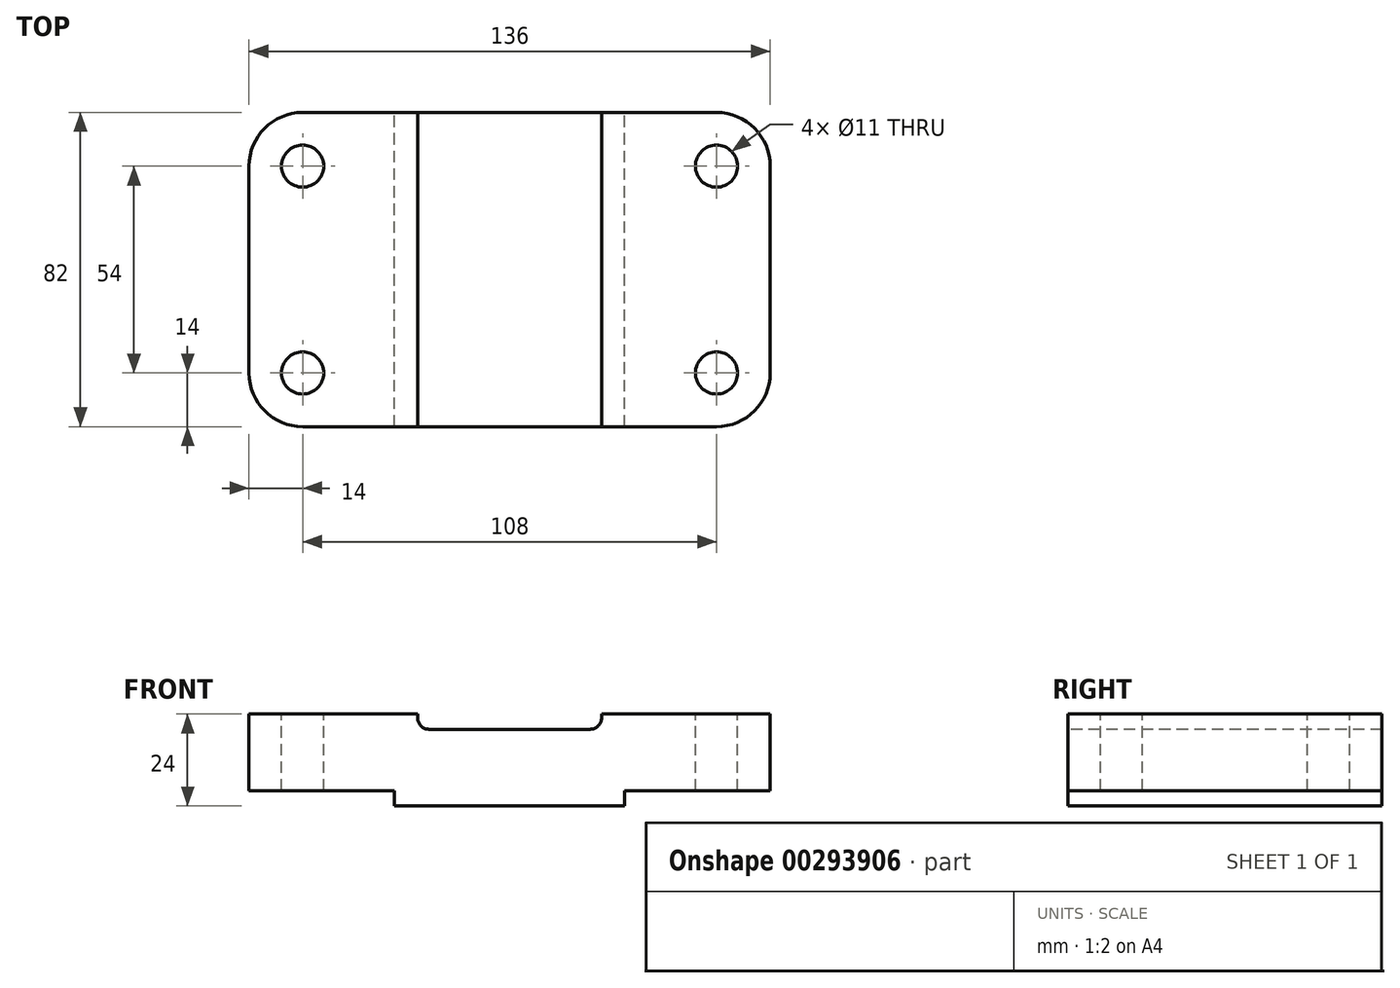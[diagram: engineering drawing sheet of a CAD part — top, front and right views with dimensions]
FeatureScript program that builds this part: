
annotation { "Feature Type Name" : "Feature", "Feature Type Description" : "" }
export const myFeature = defineFeature(function(context is Context, id is Id, definition is map)
    precondition{}
    {
        {
            var Q0;
            Q0=qCreatedBy(makeId("Top.planeOp"),FACE);
            var sketch = newSketch(context, id + "F0", { "sketchPlane" : qUnion([Q0])});
            skCircle(sketch, "E0", {"center": v(0, 0) * mm, "radius": 5.5 * mm});
            skArc(sketch, "E1", {"start": v(-14, 0) * mm, "mid": v(-9.9, -9.9) * mm, "end": v(0, -14) * mm});
            skLineSegment(sketch, "E2", {"start": v(-14, 0) * mm, "end": v(-14, 54) * mm});
            skArc(sketch, "E3", {"start": v(-14, 54) * mm, "mid": v(-9.9, 63.9) * mm, "end": v(0, 68) * mm});
            skCircle(sketch, "E4", {"center": v(0, 54) * mm, "radius": 5.5 * mm});
            skLineSegment(sketch, "E5", {"start": v(0, 68) * mm, "end": v(108, 68) * mm});
            skArc(sketch, "E6", {"start": v(108, 68) * mm, "mid": v(117.9, 63.9) * mm, "end": v(122, 54) * mm});
            skLineSegment(sketch, "E7", {"start": v(122, 54) * mm, "end": v(122, 0) * mm});
            skArc(sketch, "E8", {"start": v(122, 0) * mm, "mid": v(117.9, -9.9) * mm, "end": v(108, -14) * mm});
            skLineSegment(sketch, "E9", {"start": v(0, -14) * mm, "end": v(108, -14) * mm});
            skCircle(sketch, "E10", {"center": v(108, 54) * mm, "radius": 5.5 * mm});
            skCircle(sketch, "E11", {"center": v(108, 0) * mm, "radius": 5.5 * mm});
            skLineSegment(sketch, "E12", {"start": v(30, 68) * mm, "end": v(30, -14) * mm});
            skLineSegment(sketch, "E13", {"start": v(78, 68) * mm, "end": v(78, -14) * mm});
            skSolve(sketch);
        }
        {
            var Q0;
            Q0 = qSketchRegion(id + "F0", true);
            extrude(context, id + "F1", {"entities" : qUnion([Q0]), "oppositeDirection" : true, "depth" : 24 * mm});
        }
        {
            var Q0;
            {var subQ0=sQuery(id+"F0.wireOp",EDGE,"E12");Q0=makeQuery(id+"F0.imprint","IMPRINT",FACE,{"disambiguationData":[TD([[makeQuery(id+"F0.imprint","IMPRINT",EDGE,{"derivedFrom":subQ0}),1.0]])]});}
            extrude(context, id + "F2", {"entities" : qUnion([Q0]), "operationType" : NewBodyOperationType.REMOVE, "oppositeDirection" : true, "depth" : 4 * mm});
        }
        {
            var Q0;
            Q0=makeQuery(id+"F2.boolean.opBoolean","COPY",EDGE,{"derivedFrom":makeQuery(id+"F2.opExtrude","CAP_EDGE",EDGE,{"disambiguationData":[OSD([sQuery(id+"F0.wireOp",EDGE,"E13")])],"isStart":false})});
            var Q1;
            Q1=makeQuery(id+"F2.boolean.opBoolean","COPY",EDGE,{"derivedFrom":makeQuery(id+"F2.opExtrude","CAP_EDGE",EDGE,{"disambiguationData":[OSD([sQuery(id+"F0.wireOp",EDGE,"E12")])],"isStart":false})});
            fillet(context, id + "F3", {"entities" : qUnion([Q0, Q1]), "radius" : 3 * mm, "tangentPropagation" : true, "allowEdgeOverflow" : false});
        }
        {
            var Q0;
            Q0=makeQuery(id+"F1.opExtrude","CAP_FACE",FACE,{"disambiguationData":[OSD([sQuery(id+"F0.wireOp",EDGE,"E0"),sQuery(id+"F0.wireOp",EDGE,"E1"),sQuery(id+"F0.wireOp",EDGE,"E2"),sQuery(id+"F0.wireOp",EDGE,"E3"),sQuery(id+"F0.wireOp",EDGE,"E4"),sQuery(id+"F0.wireOp",EDGE,"E5"),sQuery(id+"F0.wireOp",EDGE,"E6"),sQuery(id+"F0.wireOp",EDGE,"E7"),sQuery(id+"F0.wireOp",EDGE,"E8"),sQuery(id+"F0.wireOp",EDGE,"E9"),sQuery(id+"F0.wireOp",EDGE,"E10"),sQuery(id+"F0.wireOp",EDGE,"E11")])],"isStart":false});
            var sketch = newSketch(context, id + "F4", { "sketchPlane" : qUnion([Q0])});
            skLineSegment(sketch, "E14", {"start": v(24, 14) * mm, "end": v(24, -68) * mm});
            skLineSegment(sketch, "E15", {"start": v(84, 14) * mm, "end": v(84, -68) * mm});
            skSolve(sketch);
        }
        {
            var Q0;
            {var subQ2=sQuery(id+"F4.wireOp",EDGE,"E14");Q0=makeQuery(id+"F4.imprint","IMPRINT",FACE,{"disambiguationData":[TD([[makeQuery(id+"F4.imprint","IMPRINT",EDGE,{"derivedFrom":subQ2}),-1.0]])]});}
            var Q1;
            {var subQ2=sQuery(id+"F4.wireOp",EDGE,"E15");Q1=makeQuery(id+"F4.imprint","IMPRINT",FACE,{"disambiguationData":[TD([[makeQuery(id+"F4.imprint","IMPRINT",EDGE,{"derivedFrom":subQ2}),1.0]])]});}
            extrude(context, id + "F5", {"entities" : qUnion([Q0, Q1]), "operationType" : NewBodyOperationType.REMOVE, "oppositeDirection" : true, "depth" : 4 * mm});
        }
    });
